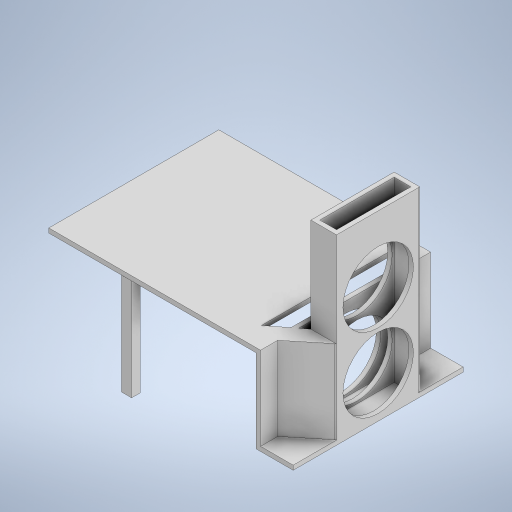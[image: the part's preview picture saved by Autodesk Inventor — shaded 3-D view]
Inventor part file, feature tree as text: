
AUTODESK INVENTOR PART (.ipt)
format: ipt  version: 2024 (Build 280153000, 153)  size: 389,120 bytes
history: native  units: in
note: dims shown in document units (in); Inventor stores cm internally (conversion verified against a paired STEP export)
features: extrude x11, sketch x9, fillet x2
ambient origin geometry x8: Origin, YZ Plane, XZ Plane, XY Plane, X Axis, Y Axis, Z Axis, Center Point
bodies: Solid1 (feature_tree)
feature tree (22):
  extrude  "Extrusion1"  Depth=0.0039in
  extrude  "Extrusion2"  Depth=0.2677in
  sketch  "Sketch3"  dims[d4=0.2283in d5=0.0079in d6=0.2677in d7=0.2283in]
  extrude  "Extrusion3"  Depth=0.2677in
  extrude  "Extrusion4"  Depth=4.5669in
  extrude  "Extrusion5"  Depth=0.1181in TaperAngle=0.0deg
  extrude  "Extrusion6"  Depth=0.1181in
  extrude  "Extrusion7"  Depth=0.1181in
  fillet  "Fillet1"  Radius=2.0945in
  fillet  "Fillet2"  Radius=1.3071in
  extrude  "Extrusion8"  Depth=4.5197in TaperAngle=0.0deg
  sketch  "Sketch8"  dims[d20=4.5197in d21=0.0in d22=4.5197in d23=0.0in]
  extrude  "Extrusion9"  Depth=0.1181in
  extrude  "Extrusion10"  Depth=0.4449in
  extrude  "Extrusion11"  Depth=0.8622in
  sketch  "Sketch1"  dims[d0=4.5276in d1=0.0039in]
  sketch  "Sketch2"  dims[d2=0.0039in d3=0.2677in]
  sketch  "Sketch4"  dims[d8=2.6969in d9=0.0in d10=4.5669in]
  sketch  "Sketch5"  dims[d11=1.9291in d12=0.1181in d13=0.0in]
  sketch  "Sketch6"  dims[d14=2.7559in d15=0.1181in]
  sketch  "Sketch7"  dims[d16=2.2126in d17=0.1181in d18=2.0945in d19=1.3071in]
  sketch  "Sketch9"  dims[d24=0.9882in d25=0.9882in d26=0.4449in d27=0.8622in d28=0.1181in d29=4.7244in d30=0.0in d31=2.2126in d32=4.7244in d33=0.9843in d34=0.9843in d35=0.9961in d36=1.9724in d37=1.874in d38=1.874in d39=0.7874in d40=0.0in d41=2.2126in d42=0.0in d43=0.0787in d44=0.0787in d45=3.5827in d46=0.1181in d47=4.5197in d48=0.0in d49=0.1181in d50=0.1181in d51=0.0in d52=2.3228in d53=0.0in d54=0.1181in d55=0.0in d56=0.0197in d57=0.0344in]
